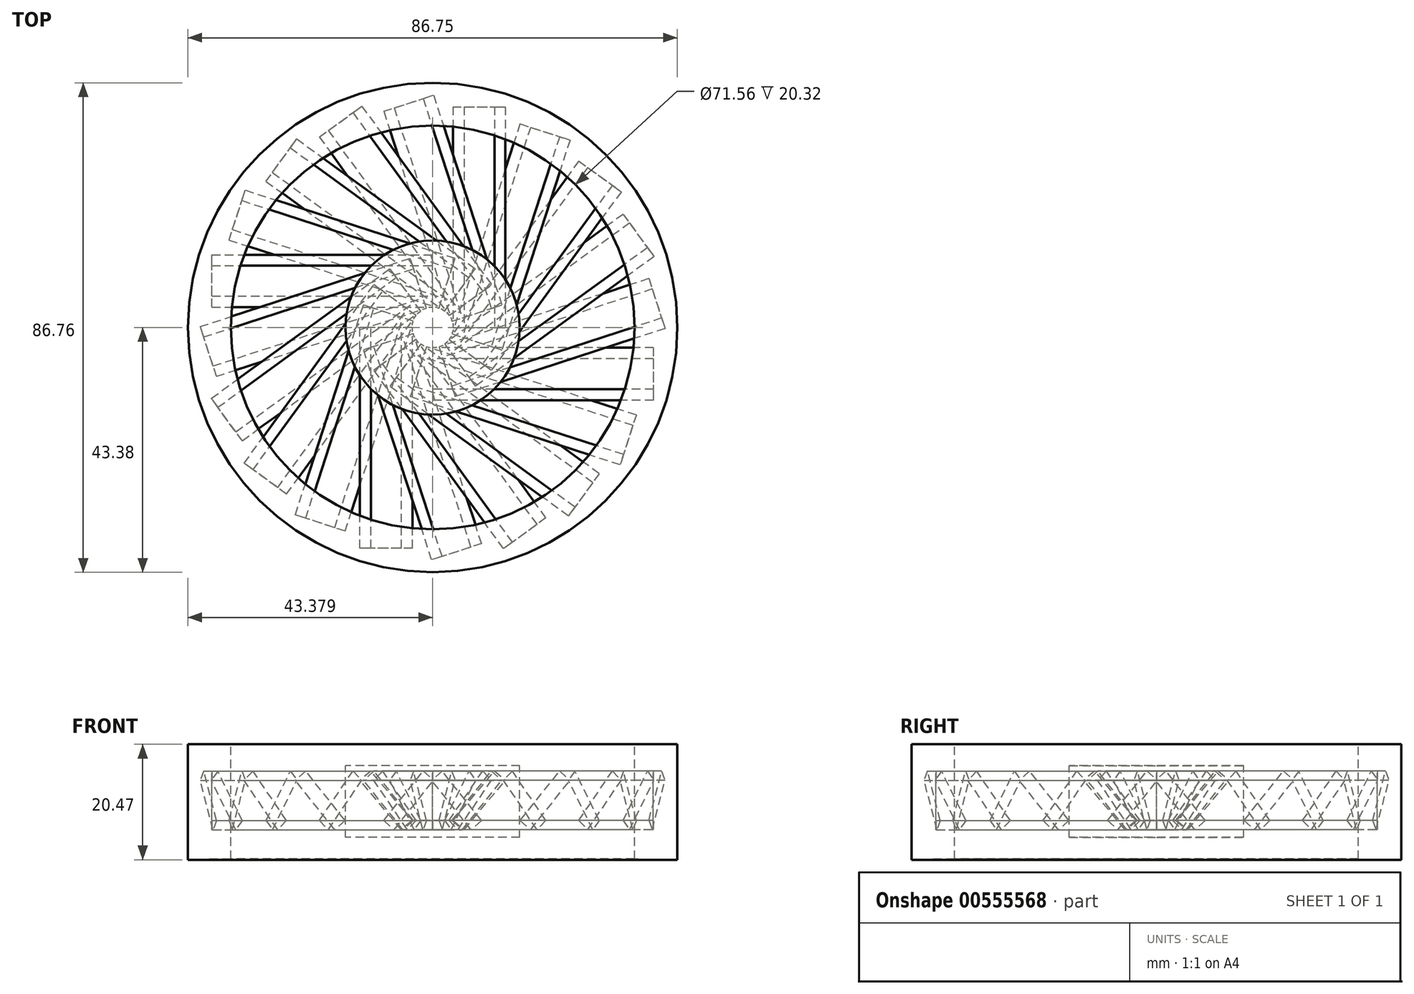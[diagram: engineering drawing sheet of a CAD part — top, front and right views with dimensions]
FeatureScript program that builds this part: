
annotation { "Feature Type Name" : "Feature", "Feature Type Description" : "" }
export const myFeature = defineFeature(function(context is Context, id is Id, definition is map)
    precondition{}
    {
        {
            var Q0;
            Q0=qCreatedBy(makeId("Front.planeOp"),FACE);
            var sketch = newSketch(context, id + "F0", { "sketchPlane" : qUnion([Q0])});
            skLineSegment(sketch, "E0", {"start": v(0, 0) * mm, "end": v(0, -12.7) * mm});
            skLineSegment(sketch, "E1", {"start": v(-20.34, 3.8) * mm, "end": v(-20.34, -16.51) * mm});
            skLineSegment(sketch, "E2", {"start": v(0, -6.35) * mm, "end": v(-20.34, -6.35) * mm});
            skLineSegment(sketch, "E3", {"start": v(-20.34, 3.8) * mm, "end": v(-27.94, 3.8) * mm});
            skLineSegment(sketch, "E4", {"start": v(-27.94, 3.8) * mm, "end": v(-27.94, -16.66) * mm});
            skLineSegment(sketch, "E5", {"start": v(-27.94, -16.66) * mm, "end": v(-20.34, -16.51) * mm});
            skLineSegment(sketch, "E6", {"start": v(15.44, 0) * mm, "end": v(15.44, -19.11) * mm});
            skLineSegment(sketch, "E7", {"start": v(0, 0) * mm, "end": v(15.44, 0) * mm});
            skLineSegment(sketch, "E8", {"start": v(0, -12.7) * mm, "end": v(15.44, -12.7) * mm});
            skLineSegment(sketch, "E9", {"start": v(15.44, -12.7) * mm, "end": v(15.44, 0) * mm});
            skSolve(sketch);
        }
        {
            var Q0;
            Q0 = qSketchRegion(id + "F0", true);
            var Q1;
            Q1=sQuery(id+"F0.wireOp",EDGE,"E6");
            revolve(context, id + "F1", {"entities" : qUnion([Q0]), "axis" : qUnion([Q1]), "revolveType" : RevolveType.FULL});
        }
        {
            var Q0;
            Q0=qCreatedBy(makeId("Front.planeOp"),FACE);
            var sketch = newSketch(context, id + "F2", { "sketchPlane" : qUnion([Q0])});
            skLineSegment(sketch, "E10.bottom", {"start": v(11.84, -9.7) * mm, "end": v(9.9, -11.34) * mm});
            skLineSegment(sketch, "E10.top", {"start": v(4.5, -0.95) * mm, "end": v(2.55, -2.58) * mm});
            skLineSegment(sketch, "E10.left", {"start": v(11.84, -9.7) * mm, "end": v(4.5, -0.95) * mm});
            skLineSegment(sketch, "E10.right", {"start": v(9.9, -11.34) * mm, "end": v(2.55, -2.58) * mm});
            skSolve(sketch);
        }
        {
            var Q0;
            Q0 = qSketchRegion(id + "F2", true);
            extrude(context, id + "F3", {"entities" : qUnion([Q0]), "depth" : 39.12 * mm, "offsetDistance" : 25.4 * mm});
        }
        {
            var Q0;
            Q0=makeQuery(id+"F3.opExtrude","SWEPT_BODY",BODY,{"disambiguationData":[OSD([sQuery(id+"F2.wireOp",EDGE,"E10.bottom"),sQuery(id+"F2.wireOp",EDGE,"E10.top"),sQuery(id+"F2.wireOp",EDGE,"E10.left"),sQuery(id+"F2.wireOp",EDGE,"E10.right")])]});
            var Q1;
            Q1=sQuery(id+"F0.wireOp",EDGE,"E9");
            circularPattern(context, id + "F4", {"entities" : qUnion([Q0]), "axis" : qUnion([Q1]), "angle" : 360 * degree, "instanceCount" : 20, "equalSpace" : true});
        }
    });
